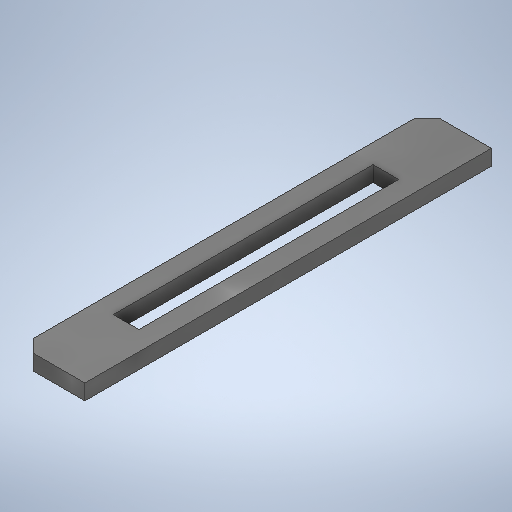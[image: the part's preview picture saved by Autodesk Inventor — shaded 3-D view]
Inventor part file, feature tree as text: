
AUTODESK INVENTOR PART (.ipt)
format: ipt  version: 2025 (Build 290162000, 162)  size: 267,264 bytes
history: native  units: in
note: dims shown in document units (in); Inventor stores cm internally (conversion verified against a paired STEP export)
features: extrude x3, sketch x3, other x2
ambient origin geometry x8: Origin, YZ Plane, XZ Plane, XY Plane, X Axis, Y Axis, Z Axis, Center Point
bodies: Solid1 (feature_tree)
feature tree (8):
  other  "Annotations"
  extrude  "Extrusion1"  Depth=0.0236in TaperAngle=0.0deg
  extrude  "Extrusion2"  Depth=0.3976in
  extrude  "Extrusion3"  Depth=0.0492in
  sketch  "Sketch1"  dims[d0=0.622in d1=0.0236in d2=0.0in]
  sketch  "Sketch2"  dims[d3=0.0394in d4=0.3976in]
  sketch  "Sketch3"  dims[d5=0.0in d6=0.0in d7=0.0492in d8=0.0492in d9=0.0197in d10=0.0197in d11=0.0197in d12=0.0197in d13=0.0in d14=0.0in d15=0.311in]
  other  "General Note 1"
